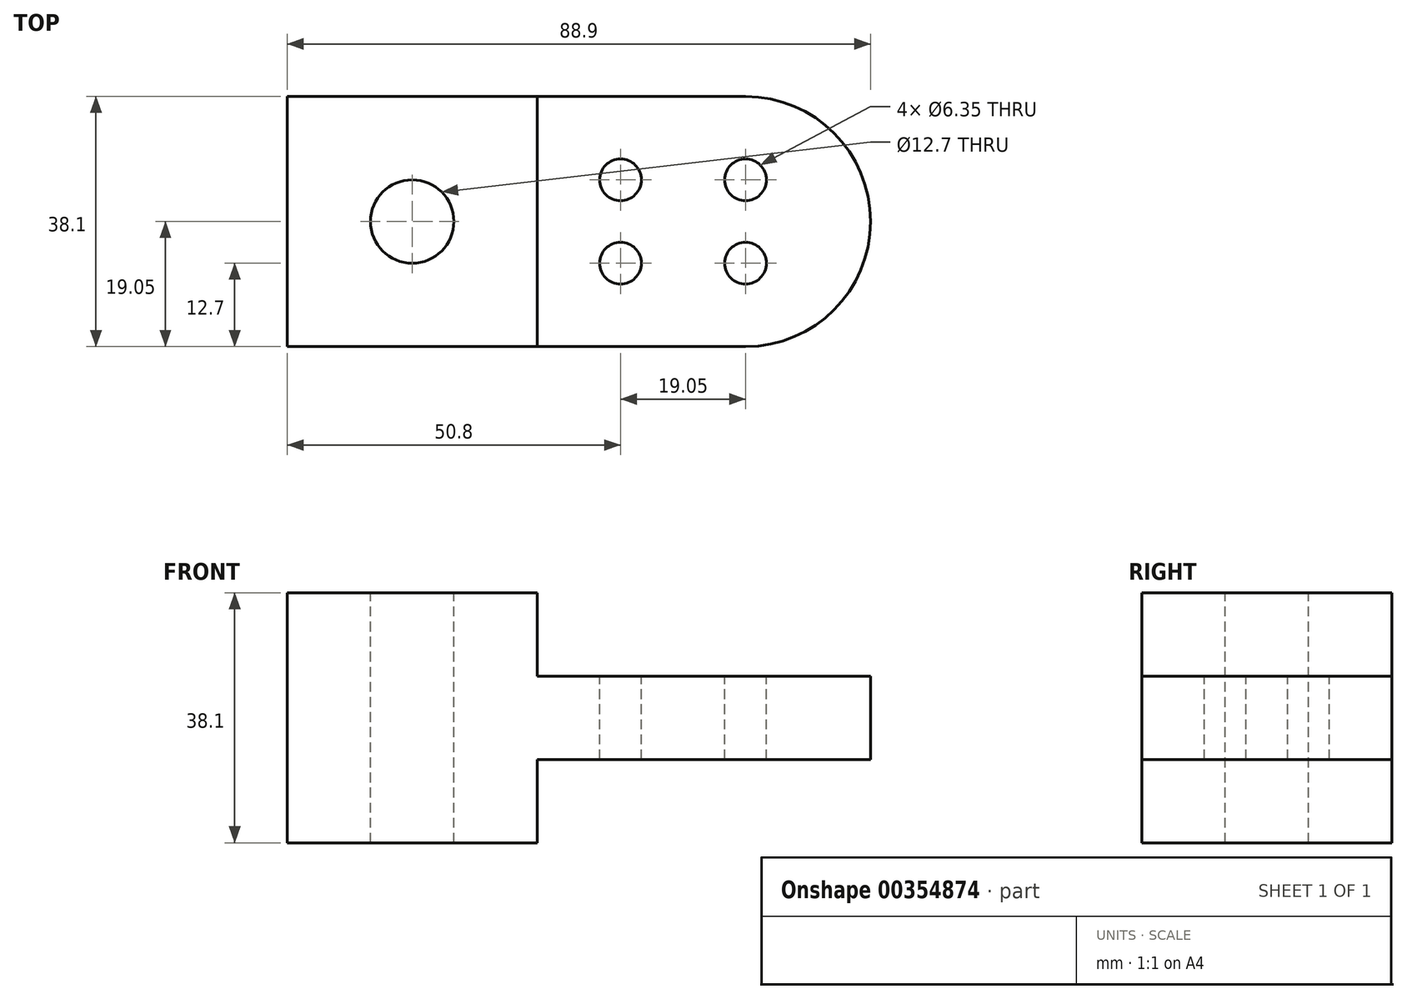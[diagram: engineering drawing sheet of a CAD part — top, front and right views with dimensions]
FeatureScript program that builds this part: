
annotation { "Feature Type Name" : "Feature", "Feature Type Description" : "" }
export const myFeature = defineFeature(function(context is Context, id is Id, definition is map)
    precondition{}
    {
        {
            var Q0;
            Q0=qCreatedBy(makeId("Top.planeOp"),FACE);
            var sketch = newSketch(context, id + "F0", { "sketchPlane" : qUnion([Q0])});
            skLineSegment(sketch, "E0", {"start": v(0, 0) * mm, "end": v(38.1, 0) * mm});
            skLineSegment(sketch, "E1", {"start": v(38.1, 0) * mm, "end": v(38.1, 38.1) * mm});
            skLineSegment(sketch, "E2", {"start": v(38.1, 38.1) * mm, "end": v(0, 38.1) * mm});
            skLineSegment(sketch, "E3", {"start": v(0, 38.1) * mm, "end": v(0, 0) * mm});
            skSolve(sketch);
        }
        {
            var Q0;
            Q0 = qSketchRegion(id + "F0", true);
            extrude(context, id + "F1", {"entities" : qUnion([Q0]), "oppositeDirection" : true, "depth" : 12.7 * mm});
        }
        {
            var Q0;
            Q0=makeQuery(id+"F1.opExtrude","CAP_FACE",FACE,{"disambiguationData":[OSD([sQuery(id+"F0.wireOp",EDGE,"E0"),sQuery(id+"F0.wireOp",EDGE,"E1"),sQuery(id+"F0.wireOp",EDGE,"E2"),sQuery(id+"F0.wireOp",EDGE,"E3")])],"isStart":true});
            var sketch = newSketch(context, id + "F2", { "sketchPlane" : qUnion([Q0])});
            skLineSegment(sketch, "E4", {"start": v(0, 0) * mm, "end": v(38.1, 0) * mm});
            skLineSegment(sketch, "E5", {"start": v(38.1, 0) * mm, "end": v(38.1, 38.1) * mm});
            skLineSegment(sketch, "E6", {"start": v(38.1, 38.1) * mm, "end": v(0, 38.1) * mm});
            skLineSegment(sketch, "E7", {"start": v(0, 38.1) * mm, "end": v(0, 0) * mm});
            skLineSegment(sketch, "E8", {"start": v(38.1, 38.1) * mm, "end": v(69.85, 38.1) * mm});
            skLineSegment(sketch, "E9", {"start": v(38.1, 0) * mm, "end": v(69.85, 0) * mm});
            skArc(sketch, "E10", {"start": v(69.85, 0) * mm, "mid": v(88.9, 19.05) * mm, "end": v(69.85, 38.1) * mm});
            skSolve(sketch);
        }
        {
            var Q0;
            Q0 = qSketchRegion(id + "F2", true);
            extrude(context, id + "F3", {"entities" : qUnion([Q0]), "operationType" : NewBodyOperationType.ADD, "depth" : 12.7 * mm});
        }
        {
            var Q0;
            Q0=makeQuery(id+"F3.opExtrude","CAP_FACE",FACE,{"disambiguationData":[OSD([sQuery(id+"F2.wireOp",EDGE,"E4"),sQuery(id+"F2.wireOp",EDGE,"E6"),sQuery(id+"F2.wireOp",EDGE,"E7"),sQuery(id+"F2.wireOp",EDGE,"E8"),sQuery(id+"F2.wireOp",EDGE,"E9"),sQuery(id+"F2.wireOp",EDGE,"E10")])],"isStart":false});
            var sketch = newSketch(context, id + "F4", { "sketchPlane" : qUnion([Q0])});
            skLineSegment(sketch, "E11", {"start": v(0, 38.1) * mm, "end": v(0, 0) * mm, "construction": true});
            skLineSegment(sketch, "E12", {"start": v(0, 38.1) * mm, "end": v(38.1, 38.1) * mm, "construction": true});
            skLineSegment(sketch, "E13", {"start": v(38.1, 38.1) * mm, "end": v(38.1, 0) * mm, "construction": true});
            skLineSegment(sketch, "E14", {"start": v(38.1, 0) * mm, "end": v(0, 0) * mm, "construction": true});
            skLineSegment(sketch, "E15", {"start": v(38.1, 38.1) * mm, "end": v(38.1, 25.4) * mm, "construction": true});
            skLineSegment(sketch, "E16", {"start": v(38.1, 25.4) * mm, "end": v(50.8, 25.4) * mm, "construction": true});
            skLineSegment(sketch, "E17", {"start": v(38.1, 0) * mm, "end": v(38.1, 12.7) * mm, "construction": true});
            skLineSegment(sketch, "E18", {"start": v(38.1, 12.7) * mm, "end": v(50.8, 12.7) * mm, "construction": true});
            skCircle(sketch, "E19", {"center": v(50.8, 25.4) * mm, "radius": 3.18 * mm});
            skCircle(sketch, "E20", {"center": v(50.8, 12.7) * mm, "radius": 3.18 * mm});
            skLineSegment(sketch, "E21", {"start": v(50.8, 12.7) * mm, "end": v(69.85, 12.7) * mm, "construction": true});
            skLineSegment(sketch, "E22", {"start": v(50.8, 25.4) * mm, "end": v(69.85, 25.4) * mm, "construction": true});
            skCircle(sketch, "E23", {"center": v(69.85, 25.4) * mm, "radius": 3.18 * mm});
            skCircle(sketch, "E24", {"center": v(69.85, 12.7) * mm, "radius": 3.18 * mm});
            skSolve(sketch);
        }
        {
            var Q0;
            Q0 = qSketchRegion(id + "F4", true);
            extrude(context, id + "F5", {"entities" : qUnion([Q0]), "operationType" : NewBodyOperationType.REMOVE, "oppositeDirection" : true, "depth" : 25.4 * mm});
        }
        {
            var Q0;
            Q0=makeQuery(id+"F3.opExtrude","CAP_FACE",FACE,{"disambiguationData":[OSD([sQuery(id+"F2.wireOp",EDGE,"E4"),sQuery(id+"F2.wireOp",EDGE,"E6"),sQuery(id+"F2.wireOp",EDGE,"E7"),sQuery(id+"F2.wireOp",EDGE,"E8"),sQuery(id+"F2.wireOp",EDGE,"E9"),sQuery(id+"F2.wireOp",EDGE,"E10")])],"isStart":false});
            var sketch = newSketch(context, id + "F6", { "sketchPlane" : qUnion([Q0])});
            skLineSegment(sketch, "E25", {"start": v(38.1, 0) * mm, "end": v(0, 0) * mm});
            skLineSegment(sketch, "E26", {"start": v(0, 0) * mm, "end": v(0, 38.1) * mm});
            skLineSegment(sketch, "E27", {"start": v(0, 38.1) * mm, "end": v(38.1, 38.1) * mm});
            skLineSegment(sketch, "E28", {"start": v(38.1, 38.1) * mm, "end": v(38.1, 0) * mm});
            skSolve(sketch);
        }
        {
            var Q0;
            Q0 = qSketchRegion(id + "F6", true);
            extrude(context, id + "F7", {"entities" : qUnion([Q0]), "operationType" : NewBodyOperationType.ADD, "depth" : 12.7 * mm});
        }
        {
            var Q0;
            Q0=makeQuery(id+"F7.opExtrude","CAP_FACE",FACE,{"disambiguationData":[OSD([sQuery(id+"F6.wireOp",EDGE,"E25"),sQuery(id+"F6.wireOp",EDGE,"E26"),sQuery(id+"F6.wireOp",EDGE,"E27"),sQuery(id+"F6.wireOp",EDGE,"E28")])],"isStart":false});
            var sketch = newSketch(context, id + "F8", { "sketchPlane" : qUnion([Q0])});
            skSolve(sketch);
        }
        {
            var Q0;
            Q0=makeQuery(id+"F8.imprint","IMPRINT",FACE,{"disambiguationData":[TD([[makeQuery(id+"F8.imprint","IMPRINT",EDGE,{"derivedFrom":makeQuery(id+"F7.opExtrude","CAP_EDGE",EDGE,{"disambiguationData":[OSD([sQuery(id+"F6.wireOp",EDGE,"E25")])],"isStart":false})}),1.0]])]});
            var sketch = newSketch(context, id + "F9", { "sketchPlane" : qUnion([Q0])});
            skLineSegment(sketch, "E29.bottom", {"start": v(0, 0) * mm, "end": v(38.1, 0) * mm, "construction": true});
            skLineSegment(sketch, "E29.top", {"start": v(0, 38.1) * mm, "end": v(38.1, 38.1) * mm, "construction": true});
            skLineSegment(sketch, "E29.left", {"start": v(0, 0) * mm, "end": v(0, 38.1) * mm, "construction": true});
            skLineSegment(sketch, "E29.right", {"start": v(38.1, 0) * mm, "end": v(38.1, 38.1) * mm, "construction": true});
            skLineSegment(sketch, "E30", {"start": v(0, 38.1) * mm, "end": v(38.1, 0) * mm, "construction": true});
            skLineSegment(sketch, "E31", {"start": v(0, 0) * mm, "end": v(38.1, 38.1) * mm, "construction": true});
            skCircle(sketch, "E32", {"center": v(19.05, 19.05) * mm, "radius": 6.35 * mm});
            skSolve(sketch);
        }
        {
            var Q0;
            Q0 = qSketchRegion(id + "F9", true);
            extrude(context, id + "F10", {"entities" : qUnion([Q0]), "operationType" : NewBodyOperationType.REMOVE, "oppositeDirection" : true, "depth" : 76.2 * mm});
        }
    });
